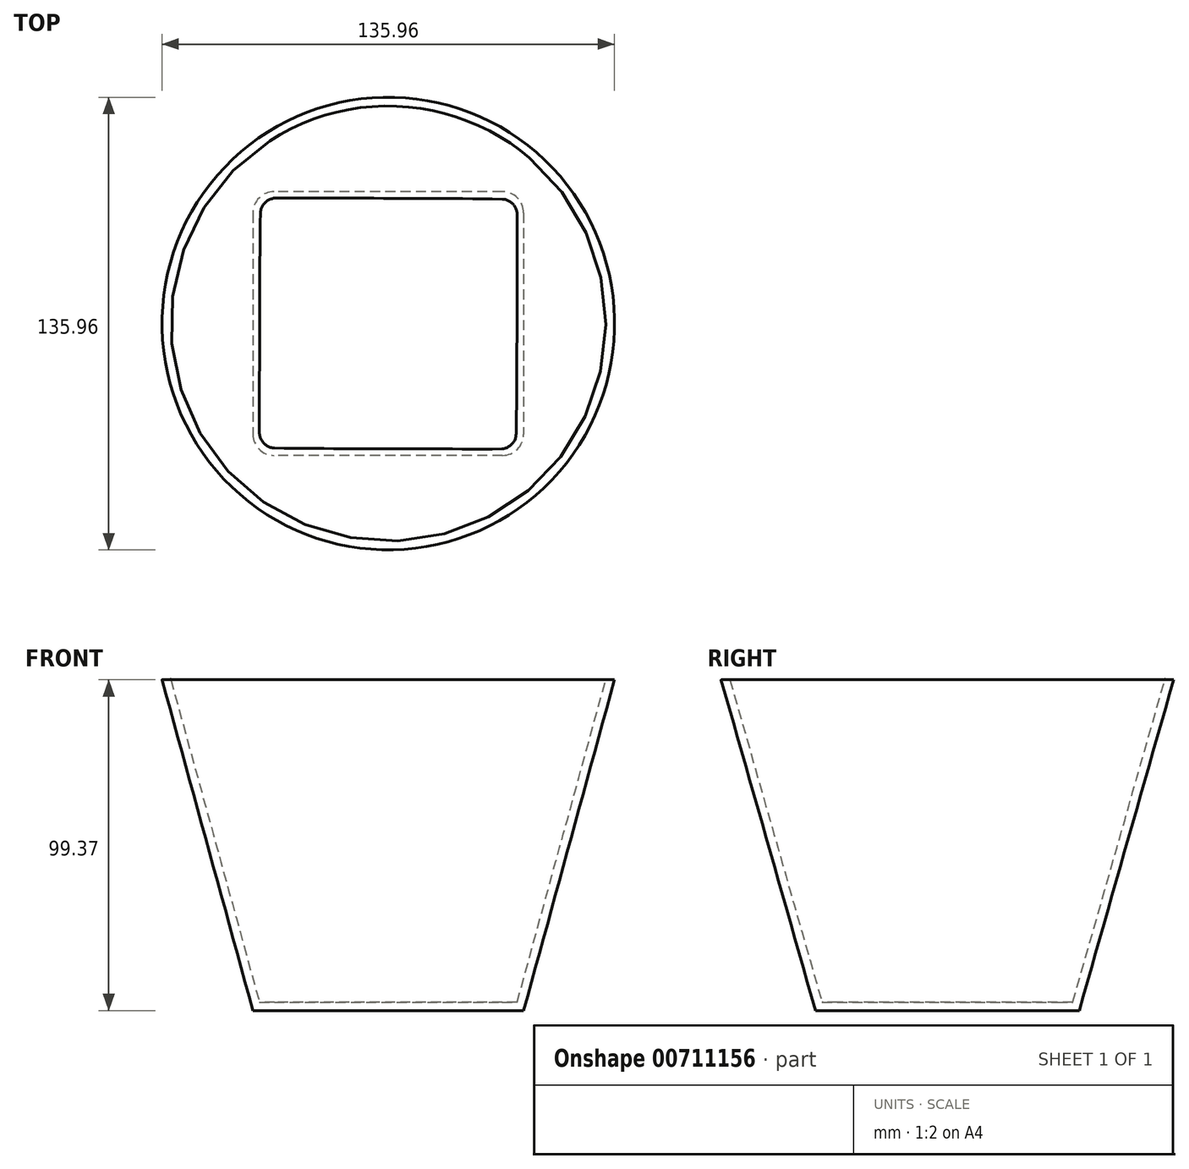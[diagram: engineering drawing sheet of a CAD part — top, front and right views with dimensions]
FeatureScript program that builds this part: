
annotation { "Feature Type Name" : "Feature", "Feature Type Description" : "" }
export const myFeature = defineFeature(function(context is Context, id is Id, definition is map)
    precondition{}
    {
        {
            var Q0;
            Q0=qCreatedBy(makeId("Front.planeOp"),FACE);
            var sketch = newSketch(context, id + "F0", { "sketchPlane" : qUnion([Q0])});
            skLineSegment(sketch, "E0.bottom", {"start": v(0, 0) * mm, "end": v(0, 0) * mm});
            skLineSegment(sketch, "E0.top", {"start": v(0, 0) * mm, "end": v(0, 0) * mm});
            skLineSegment(sketch, "E0.left", {"start": v(0, 0) * mm, "end": v(0, 0) * mm});
            skLineSegment(sketch, "E0.right", {"start": v(0, 0) * mm, "end": v(0, 0) * mm});
            skLineSegment(sketch, "E1.bottom", {"start": v(88.16, 10.94) * mm, "end": v(0, 10.94) * mm});
            skLineSegment(sketch, "E1.top", {"start": v(88.16, 0) * mm, "end": v(0, 0) * mm});
            skLineSegment(sketch, "E1.left", {"start": v(88.16, 10.94) * mm, "end": v(88.16, 0) * mm});
            skLineSegment(sketch, "E1.right", {"start": v(0, 10.94) * mm, "end": v(0, 0) * mm});
            skSolve(sketch);
        }
        {
            var Q0;
            Q0=makeQuery(id+"F0.imprint","IMPRINT",FACE,{"disambiguationData":[TD([[makeQuery(id+"F0.imprint","IMPRINT",EDGE,{"derivedFrom":sQuery(id+"F0.wireOp",EDGE,"E1.bottom")}),1.0]])]});
            extrude(context, id + "F1", {"entities" : qUnion([Q0]), "depth" : 63.73 * mm, "offsetDistance" : 25.4 * mm});
        }
        {
            var Q0;
            Q0=makeQuery(id+"F1.opExtrude","SWEPT_BODY",BODY,{"disambiguationData":[OSD([sQuery(id+"F0.wireOp",EDGE,"E1.bottom"),sQuery(id+"F0.wireOp",EDGE,"E1.top"),sQuery(id+"F0.wireOp",EDGE,"E1.left"),sQuery(id+"F0.wireOp",EDGE,"E1.right")])]});
            deleteBodies(context, id + "F2", {"entities" : qUnion([Q0])});
        }
        {
            var Q0;
            Q0=qCreatedBy(makeId("Top.planeOp"),FACE);
            var sketch = newSketch(context, id + "F3", { "sketchPlane" : qUnion([Q0])});
            skLineSegment(sketch, "E2.bottom", {"start": v(34.31, 39.6) * mm, "end": v(-34.31, 39.6) * mm});
            skLineSegment(sketch, "E2.top", {"start": v(34.31, -39.6) * mm, "end": v(-34.31, -39.6) * mm});
            skLineSegment(sketch, "E2.left", {"start": v(40.66, 33.26) * mm, "end": v(40.66, -33.26) * mm});
            skLineSegment(sketch, "E2.right", {"start": v(-40.66, 33.26) * mm, "end": v(-40.66, -33.26) * mm});
            skPoint(sketch, "E2.middle", {"position": v(0, 0) * mm});
            skPoint(sketch, "E3.visualSharp", {"position": v(40.66, 39.6) * mm});
            skArc(sketch, "E3.filletArc", {"start": v(40.66, 33.26) * mm, "mid": v(38.8, 37.75) * mm, "end": v(34.31, 39.6) * mm});
            skPoint(sketch, "E4.visualSharp", {"position": v(40.66, -39.6) * mm});
            skArc(sketch, "E4.filletArc", {"start": v(34.31, -39.6) * mm, "mid": v(38.8, -37.75) * mm, "end": v(40.66, -33.26) * mm});
            skPoint(sketch, "E5.visualSharp", {"position": v(-40.66, -39.6) * mm});
            skArc(sketch, "E5.filletArc", {"start": v(-40.66, -33.26) * mm, "mid": v(-38.8, -37.75) * mm, "end": v(-34.31, -39.6) * mm});
            skPoint(sketch, "E6.visualSharp", {"position": v(-40.66, 39.6) * mm});
            skArc(sketch, "E6.filletArc", {"start": v(-34.31, 39.6) * mm, "mid": v(-38.8, 37.75) * mm, "end": v(-40.66, 33.26) * mm});
            skSolve(sketch);
        }
        {
            var Q0;
            Q0=qCreatedBy(makeId("Top.planeOp"),FACE);
            cPlane(context, id + "F4", {"entities" : qUnion([Q0]), "cplaneType" : CPlaneType.OFFSET, "offset" : 99.37 * mm, "width" : 152.4 * mm, "height" : 152.4 * mm});
        }
        {
            var Q0;
            Q0=qCreatedBy(id+"F4.planeOp",FACE);
            var sketch = newSketch(context, id + "F5", { "sketchPlane" : qUnion([Q0])});
            skCircle(sketch, "E7", {"center": v(0, 0) * mm, "radius": 67.98 * mm});
            skSolve(sketch);
        }
        {
            var Q0;
            Q0=makeQuery(id+"F3.imprint","IMPRINT",FACE,{"disambiguationData":[TD([[makeQuery(id+"F3.imprint","IMPRINT",EDGE,{"derivedFrom":sQuery(id+"F3.wireOp",EDGE,"E2.bottom")}),1.0]])]});
            var Q1;
            Q1=makeQuery(id+"F5.imprint","IMPRINT",FACE,{"disambiguationData":[TD([[makeQuery(id+"F5.imprint","IMPRINT",EDGE,{"derivedFrom":sQuery(id+"F5.wireOp",EDGE,"E7")}),1.0]])]});
            loft(context, id + "F6", {"sheetProfilesArray" : [{ "sheetProfileEntities" : qUnion([Q0]) }, { "sheetProfileEntities" : qUnion([Q1]) }]});
        }
        {
            var Q0;
            Q0=makeQuery(id+"F6.opLoft","CAP_FACE",FACE,{"disambiguationData":[OSD([makeQuery(id+"F5.imprint","IMPRINT",FACE,{"disambiguationData":[TD([[makeQuery(id+"F5.imprint","IMPRINT",EDGE,{"derivedFrom":sQuery(id+"F5.wireOp",EDGE,"E7")}),1.0]])]})])],"isStart":true});
            shell(context, id + "F7", {"entities" : qUnion([Q0]), "thickness" : 2.54 * mm});
        }
    });
